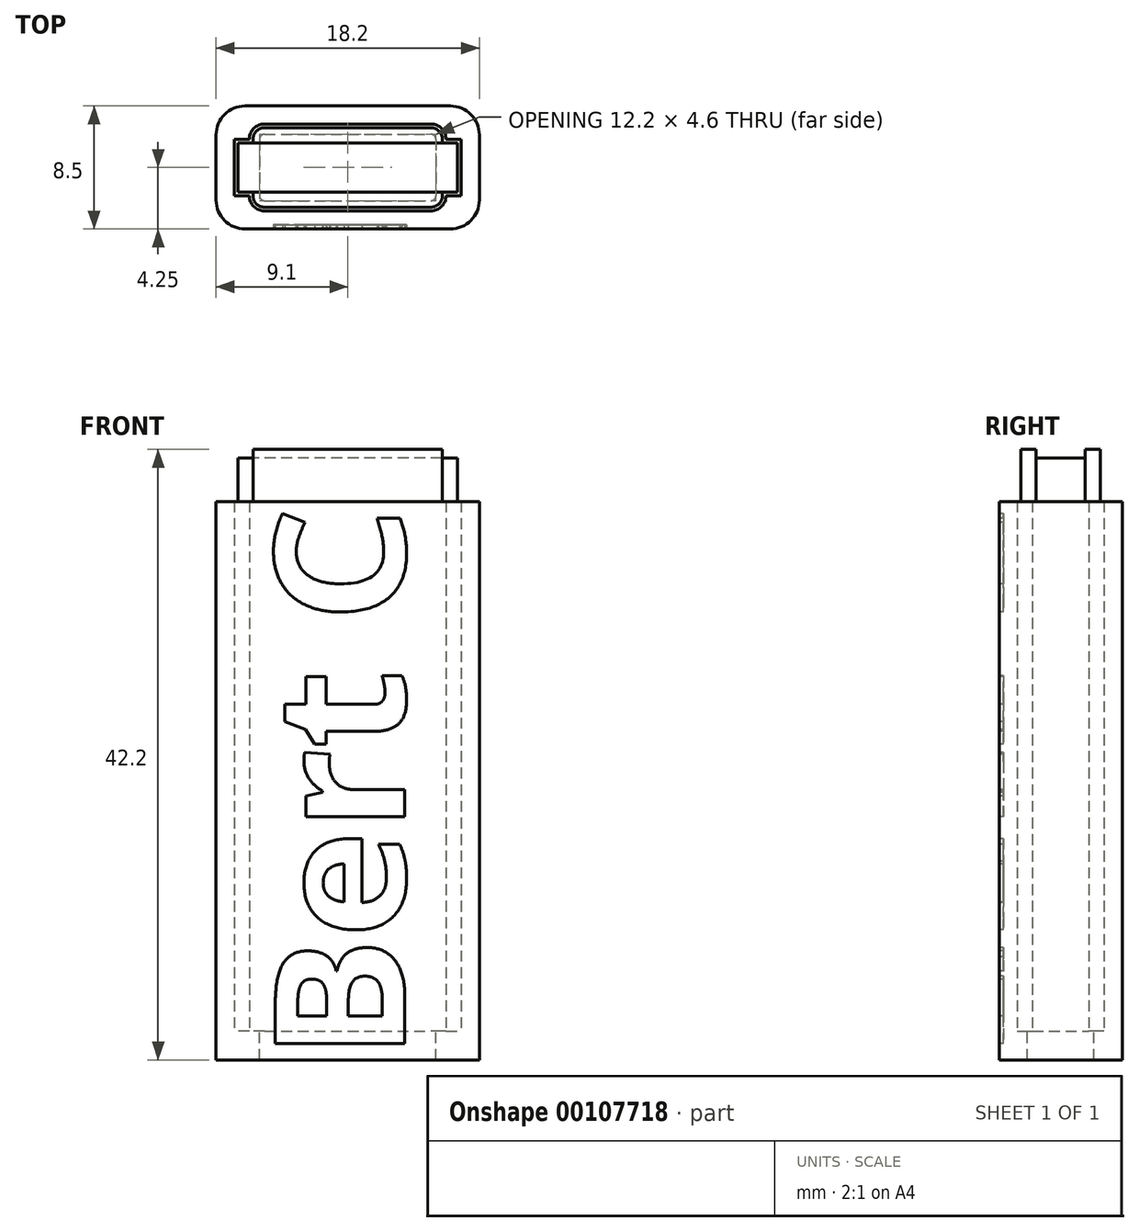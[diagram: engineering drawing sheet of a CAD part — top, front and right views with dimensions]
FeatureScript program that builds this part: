
annotation { "Feature Type Name" : "Feature", "Feature Type Description" : "" }
export const myFeature = defineFeature(function(context is Context, id is Id, definition is map)
    precondition{}
    {
        {
            var Q0;
            Q0=qCreatedBy(makeId("Top.planeOp"),FACE);
            var sketch = newSketch(context, id + "F0", { "sketchPlane" : qUnion([Q0])});
            skLineSegment(sketch, "E0.bottom", {"start": v(-5.75, 2.1) * mm, "end": v(5.75, 2.1) * mm});
            skLineSegment(sketch, "E0.top", {"start": v(-5.75, -2.3) * mm, "end": v(5.75, -2.3) * mm});
            skLineSegment(sketch, "E0.left", {"start": v(-6, 1.85) * mm, "end": v(-6, 0.2) * mm});
            skLineSegment(sketch, "E0.right", {"start": v(6, 1.85) * mm, "end": v(6, 0.2) * mm});
            skPoint(sketch, "E1.visualSharp", {"position": v(-6, 2.1) * mm});
            skArc(sketch, "E1.filletArc", {"start": v(-5.75, 2.1) * mm, "mid": v(-5.93, 2.03) * mm, "end": v(-6, 1.85) * mm});
            skPoint(sketch, "E2.visualSharp", {"position": v(-6, -2.3) * mm});
            skArc(sketch, "E2.filletArc", {"start": v(-6, -2.05) * mm, "mid": v(-5.93, -2.23) * mm, "end": v(-5.75, -2.3) * mm});
            skPoint(sketch, "E3.visualSharp", {"position": v(6, 2.1) * mm});
            skArc(sketch, "E3.filletArc", {"start": v(6, 1.85) * mm, "mid": v(5.93, 2.03) * mm, "end": v(5.75, 2.1) * mm});
            skPoint(sketch, "E4.visualSharp", {"position": v(6, -2.3) * mm});
            skArc(sketch, "E4.filletArc", {"start": v(5.75, -2.3) * mm, "mid": v(5.93, -2.23) * mm, "end": v(6, -2.05) * mm});
            skPoint(sketch, "E5", {"position": v(-6, -0.1) * mm});
            skPoint(sketch, "E6", {"position": v(6, -0.1) * mm});
            skLineSegment(sketch, "E7", {"start": v(-6, -0.1) * mm, "end": v(-7.05, -0.1) * mm});
            skLineSegment(sketch, "E8", {"start": v(6, -0.1) * mm, "end": v(7.05, -0.1) * mm});
            skLineSegment(sketch, "E9", {"start": v(-7.05, -0.1) * mm, "end": v(-7.05, 0.2) * mm});
            skLineSegment(sketch, "E10", {"start": v(-7.05, 0.2) * mm, "end": v(-6, 0.2) * mm});
            skLineSegment(sketch, "E11", {"start": v(-7.05, -0.1) * mm, "end": v(-7.05, -0.4) * mm});
            skLineSegment(sketch, "E12", {"start": v(-7.05, -0.4) * mm, "end": v(-6, -0.4) * mm});
            skLineSegment(sketch, "E13", {"start": v(7.05, -0.1) * mm, "end": v(7.05, -0.4) * mm});
            skLineSegment(sketch, "E14", {"start": v(7.05, -0.4) * mm, "end": v(6, -0.4) * mm});
            skLineSegment(sketch, "E15", {"start": v(7.05, -0.1) * mm, "end": v(7.05, 0.2) * mm});
            skLineSegment(sketch, "E16", {"start": v(7.05, 0.2) * mm, "end": v(6, 0.2) * mm});
            skPoint(sketch, "E17.end.orphan", {"position": v(-7.05, 2.1) * mm});
            skPoint(sketch, "E18.orphan", {"position": v(-7.05, -2.3) * mm});
            skPoint(sketch, "E19.end.orphan", {"position": v(7.05, 2.1) * mm});
            skPoint(sketch, "E20.orphan", {"position": v(7.05, -2.3) * mm});
            skLineSegment(sketch, "E21", {"start": v(-6, 0.2) * mm, "end": v(-6, -0.4) * mm});
            skLineSegment(sketch, "E22", {"start": v(-6, -0.4) * mm, "end": v(-6, -2.05) * mm});
            skLineSegment(sketch, "E23", {"start": v(6, -0.4) * mm, "end": v(6, -2.05) * mm});
            skLineSegment(sketch, "E24", {"start": v(6, 0.2) * mm, "end": v(6, -0.4) * mm});
            skArc(sketch, "E25.0", {"start": v(-5.75, 2.9) * mm, "mid": v(-6.5, 2.6) * mm, "end": v(-6.8, 1.85) * mm});
            skLineSegment(sketch, "E25.1", {"start": v(-5.75, 2.9) * mm, "end": v(5.75, 2.9) * mm});
            skArc(sketch, "E25.2", {"start": v(6.8, 1.85) * mm, "mid": v(6.5, 2.6) * mm, "end": v(5.75, 2.9) * mm});
            skLineSegment(sketch, "E25.3", {"start": v(6.8, 1.85) * mm, "end": v(6.8, 1) * mm});
            skLineSegment(sketch, "E25.5", {"start": v(-6.8, 1.85) * mm, "end": v(-6.8, 1) * mm});
            skLineSegment(sketch, "E25.6", {"start": v(7.85, 0) * mm, "end": v(7.85, 1.85) * mm});
            skLineSegment(sketch, "E25.7", {"start": v(7.85, 0) * mm, "end": v(7.85, -2.05) * mm});
            skLineSegment(sketch, "E25.9", {"start": v(-7.85, 0) * mm, "end": v(-7.85, -2.05) * mm});
            skLineSegment(sketch, "E25.10", {"start": v(-7.85, 0) * mm, "end": v(-7.85, 1.85) * mm});
            skLineSegment(sketch, "E25.12", {"start": v(-6.8, -1.2) * mm, "end": v(-6.8, -2.05) * mm});
            skArc(sketch, "E25.13", {"start": v(-6.8, -2.05) * mm, "mid": v(-6.5, -2.8) * mm, "end": v(-5.75, -3.1) * mm});
            skLineSegment(sketch, "E25.14", {"start": v(-5.75, -3.1) * mm, "end": v(5.75, -3.1) * mm});
            skArc(sketch, "E25.15", {"start": v(5.75, -3.1) * mm, "mid": v(6.5, -2.8) * mm, "end": v(6.8, -2.05) * mm});
            skLineSegment(sketch, "E25.16", {"start": v(6.8, -1.2) * mm, "end": v(6.8, -2.05) * mm});
            skLineSegment(sketch, "E26.0", {"start": v(-7.1, -4.35) * mm, "end": v(7.1, -4.35) * mm});
            skLineSegment(sketch, "E27.0", {"start": v(-7.1, 4.15) * mm, "end": v(7.1, 4.15) * mm});
            skLineSegment(sketch, "E28.0", {"start": v(-9.1, -2.35) * mm, "end": v(-9.1, 2.15) * mm});
            skLineSegment(sketch, "E29.0", {"start": v(9.1, -2.35) * mm, "end": v(9.1, 2.15) * mm});
            skPoint(sketch, "E30.visualSharp", {"position": v(-9.1, 4.15) * mm});
            skArc(sketch, "E30.filletArc", {"start": v(-7.1, 4.15) * mm, "mid": v(-8.51, 3.56) * mm, "end": v(-9.1, 2.15) * mm});
            skPoint(sketch, "E31.visualSharp", {"position": v(-9.1, -4.35) * mm});
            skArc(sketch, "E31.filletArc", {"start": v(-9.1, -2.35) * mm, "mid": v(-8.51, -3.76) * mm, "end": v(-7.1, -4.35) * mm});
            skPoint(sketch, "E32.visualSharp", {"position": v(9.1, -4.35) * mm});
            skArc(sketch, "E32.filletArc", {"start": v(7.1, -4.35) * mm, "mid": v(8.51, -3.76) * mm, "end": v(9.1, -2.35) * mm});
            skPoint(sketch, "E33.visualSharp", {"position": v(9.1, 4.15) * mm});
            skArc(sketch, "E33.filletArc", {"start": v(9.1, 2.15) * mm, "mid": v(8.51, 3.56) * mm, "end": v(7.1, 4.15) * mm});
            skLineSegment(sketch, "E34", {"start": v(-6.8, 1) * mm, "end": v(-6.8, -1.2) * mm});
            skLineSegment(sketch, "E35", {"start": v(6.8, 1) * mm, "end": v(6.8, -1.2) * mm});
            skArc(sketch, "E36.0", {"start": v(-6.1, -2.05) * mm, "mid": v(-6, -2.3) * mm, "end": v(-5.75, -2.4) * mm});
            skLineSegment(sketch, "E36.1", {"start": v(6.1, 1.85) * mm, "end": v(6.1, 0.4) * mm});
            skLineSegment(sketch, "E36.2", {"start": v(6.1, 0.4) * mm, "end": v(6.1, -0.4) * mm});
            skLineSegment(sketch, "E36.3", {"start": v(6.1, -0.4) * mm, "end": v(6.1, -2.05) * mm});
            skArc(sketch, "E36.4", {"start": v(5.75, -2.4) * mm, "mid": v(6, -2.3) * mm, "end": v(6.1, -2.05) * mm});
            skArc(sketch, "E36.5", {"start": v(6.1, 1.85) * mm, "mid": v(6, 2.1) * mm, "end": v(5.75, 2.2) * mm});
            skLineSegment(sketch, "E36.6", {"start": v(-5.75, -2.4) * mm, "end": v(5.75, -2.4) * mm});
            skLineSegment(sketch, "E36.7", {"start": v(-5.75, 2.2) * mm, "end": v(5.75, 2.2) * mm});
            skArc(sketch, "E36.8", {"start": v(-5.75, 2.2) * mm, "mid": v(-6, 2.1) * mm, "end": v(-6.1, 1.85) * mm});
            skLineSegment(sketch, "E36.9", {"start": v(-6.1, 1.85) * mm, "end": v(-6.1, 0.4) * mm});
            skLineSegment(sketch, "E36.10", {"start": v(-6.1, 0.4) * mm, "end": v(-6.1, -0.4) * mm});
            skLineSegment(sketch, "E36.11", {"start": v(-6.1, -0.4) * mm, "end": v(-6.1, -2.05) * mm});
            skLineSegment(sketch, "E37", {"start": v(-6.8, -2.05) * mm, "end": v(-7.85, -2.05) * mm});
            skLineSegment(sketch, "E38", {"start": v(-6.8, 1.85) * mm, "end": v(-7.85, 1.85) * mm});
            skLineSegment(sketch, "E39", {"start": v(6.8, 1.85) * mm, "end": v(7.85, 1.85) * mm});
            skLineSegment(sketch, "E40", {"start": v(6.8, -2.05) * mm, "end": v(7.85, -2.05) * mm});
            skPoint(sketch, "E41.orphan", {"position": v(-7.85, -1.2) * mm});
            skPoint(sketch, "E42.orphan", {"position": v(-7.85, 1) * mm});
            skPoint(sketch, "E43.orphan", {"position": v(7.85, 1) * mm});
            skPoint(sketch, "E44.orphan", {"position": v(7.85, -1.2) * mm});
            skSolve(sketch);
        }
        {
            var Q0;
            Q0=makeQuery(id+"F0.imprint","IMPRINT",FACE,{"disambiguationData":[TD([[makeQuery(id+"F0.imprint","IMPRINT",EDGE,{"derivedFrom":sQuery(id+"F0.wireOp",EDGE,"E25.0")}),-1.0]])]});
            extrude(context, id + "F1", {"entities" : qUnion([Q0]), "depth" : 36.6 * mm});
        }
        {
            var Q0;
            {var subQ4=sQuery(id+"F0.wireOp",EDGE,"E9");Q0=makeQuery(id+"F0.imprint","IMPRINT",FACE,{"disambiguationData":[TD([[makeQuery(id+"F0.imprint","IMPRINT",EDGE,{"derivedFrom":subQ4}),1.0]])]});}
            var Q1;
            {var subQ0=sQuery(id+"F0.wireOp",EDGE,"E9");Q1=makeQuery(id+"F0.imprint","IMPRINT",FACE,{"disambiguationData":[TD([[makeQuery(id+"F0.imprint","IMPRINT",EDGE,{"derivedFrom":subQ0}),-1.0]])]});}
            var Q2;
            {var subQ0=sQuery(id+"F0.wireOp",EDGE,"E11");Q2=makeQuery(id+"F0.imprint","IMPRINT",FACE,{"disambiguationData":[TD([[makeQuery(id+"F0.imprint","IMPRINT",EDGE,{"derivedFrom":subQ0}),1.0]])]});}
            var Q3;
            {var subQ0=sQuery(id+"F0.wireOp",EDGE,"E15");Q3=makeQuery(id+"F0.imprint","IMPRINT",FACE,{"disambiguationData":[TD([[makeQuery(id+"F0.imprint","IMPRINT",EDGE,{"derivedFrom":subQ0}),1.0]])]});}
            var Q4;
            {var subQ0=sQuery(id+"F0.wireOp",EDGE,"E13");Q4=makeQuery(id+"F0.imprint","IMPRINT",FACE,{"disambiguationData":[TD([[makeQuery(id+"F0.imprint","IMPRINT",EDGE,{"derivedFrom":subQ0}),-1.0]])]});}
            var Q5;
            {var subQ7=sQuery(id+"F0.wireOp",EDGE,"E13");Q5=makeQuery(id+"F0.imprint","IMPRINT",FACE,{"disambiguationData":[TD([[makeQuery(id+"F0.imprint","IMPRINT",EDGE,{"derivedFrom":subQ7}),1.0]])]});}
            var Q6;
            Q6=makeQuery(id+"F0.imprint","IMPRINT",FACE,{"disambiguationData":[TD([[makeQuery(id+"F0.imprint","IMPRINT",EDGE,{"derivedFrom":sQuery(id+"F0.wireOp",EDGE,"E25.0")}),-1.0]])]});
            var Q7;
            {var subQ1=sQuery(id+"F0.wireOp",EDGE,"E25.12");Q7=makeQuery(id+"F0.imprint","IMPRINT",FACE,{"disambiguationData":[TD([[makeQuery(id+"F0.imprint","IMPRINT",EDGE,{"derivedFrom":subQ1}),1.0]])]});}
            var Q8;
            {var subQ0=sQuery(id+"F0.wireOp",EDGE,"E36.10");var subQ1=sQuery(id+"F0.wireOp",EDGE,"E7");var subQ2=makeQuery(id+"F0.imprint","INTERSECT",VERTEX,{"derivedFrom":[subQ1,subQ0]});Q8=makeQuery(id+"F0.imprint","IMPRINT",FACE,{"disambiguationData":[TD([[makeQuery(id+"F0.imprint","IMPRINT",EDGE,{"disambiguationData":[TD([[subQ2,-1.0]])],"derivedFrom":subQ1}),1.0]])]});}
            var Q9;
            {var subQ0=sQuery(id+"F0.wireOp",EDGE,"E36.10");var subQ1=sQuery(id+"F0.wireOp",EDGE,"E7");var subQ2=makeQuery(id+"F0.imprint","INTERSECT",VERTEX,{"derivedFrom":[subQ1,subQ0]});Q9=makeQuery(id+"F0.imprint","IMPRINT",FACE,{"disambiguationData":[TD([[makeQuery(id+"F0.imprint","IMPRINT",EDGE,{"disambiguationData":[TD([[subQ2,-1.0]])],"derivedFrom":subQ1}),-1.0]])]});}
            var Q10;
            Q10=makeQuery(id+"F0.imprint","IMPRINT",FACE,{"disambiguationData":[TD([[makeQuery(id+"F0.imprint","IMPRINT",EDGE,{"derivedFrom":sQuery(id+"F0.wireOp",EDGE,"E25.0")}),1.0]])]});
            var Q11;
            {var subQ0=sQuery(id+"F0.wireOp",EDGE,"E36.2");var subQ1=sQuery(id+"F0.wireOp",EDGE,"E8");var subQ2=makeQuery(id+"F0.imprint","INTERSECT",VERTEX,{"derivedFrom":[subQ1,subQ0]});Q11=makeQuery(id+"F0.imprint","IMPRINT",FACE,{"disambiguationData":[TD([[makeQuery(id+"F0.imprint","IMPRINT",EDGE,{"disambiguationData":[TD([[subQ2,-1.0]])],"derivedFrom":subQ1}),1.0]])]});}
            var Q12;
            {var subQ0=sQuery(id+"F0.wireOp",EDGE,"E36.2");var subQ1=sQuery(id+"F0.wireOp",EDGE,"E8");var subQ2=makeQuery(id+"F0.imprint","INTERSECT",VERTEX,{"derivedFrom":[subQ1,subQ0]});Q12=makeQuery(id+"F0.imprint","IMPRINT",FACE,{"disambiguationData":[TD([[makeQuery(id+"F0.imprint","IMPRINT",EDGE,{"disambiguationData":[TD([[subQ2,-1.0]])],"derivedFrom":subQ1}),-1.0]])]});}
            extrude(context, id + "F2", {"entities" : qUnion([Q0, Q1, Q2, Q3, Q4, Q5, Q6, Q7, Q8, Q9, Q10, Q11, Q12]), "operationType" : NewBodyOperationType.ADD, "oppositeDirection" : true, "depth" : 2 * mm});
        }
        {
            var Q0;
            {var subQ0=sQuery(id+"F0.wireOp",EDGE,"E26.0");Q0=makeQuery(id+"F2.boolean.opBoolean","MERGE",FACE,{"derivedFrom":[makeQuery(id+"F1.opExtrude","SWEPT_FACE",FACE,{"disambiguationData":[OSD([subQ0])]}),makeQuery(id+"F2.opExtrude","SWEPT_FACE",FACE,{"disambiguationData":[OSD([subQ0])]})]});}
            var sketch = newSketch(context, id + "F3", { "sketchPlane" : qUnion([Q0])});
            skLineSegment(sketch, "E45.1", {"start": v(-7.1, 36.6) * mm, "end": v(7.1, 36.6) * mm});
            skLineSegment(sketch, "E45.2", {"start": v(-7.1, 36.6) * mm, "end": v(-7.1, -2) * mm});
            skLineSegment(sketch, "E45.3", {"start": v(7.1, 36.6) * mm, "end": v(7.1, -2) * mm});
            skLineSegment(sketch, "E45.4", {"start": v(-7.1, -2) * mm, "end": v(7.1, -2) * mm});
            skText(sketch, "E46", { "text": "Bert C\n", "fontName": "OpenSans-Bold.ttf"});
            const initialGuessF3  = {"E46": [0.00395, -0.002, 0, 1, 0.00903]};
            skSetInitialGuess(sketch, initialGuessF3);
            skSolve(sketch);
        }
        {
            var Q0;
            Q0=makeQuery(id+"F3.imprint","IMPRINT",FACE,{"disambiguationData":[TD([[makeQuery(id+"F3.imprint","IMPRINT",EDGE,{"derivedFrom":sQuery(id+"F3.wireOp",EDGE,"E46.sketch_text.stroke-76")}),-1.0]])]});
            var Q1;
            Q1=makeQuery(id+"F3.imprint","IMPRINT",FACE,{"disambiguationData":[TD([[makeQuery(id+"F3.imprint","IMPRINT",EDGE,{"derivedFrom":sQuery(id+"F3.wireOp",EDGE,"E46.sketch_text.stroke-58")}),-1.0]])]});
            var Q2;
            Q2=makeQuery(id+"F3.imprint","IMPRINT",FACE,{"disambiguationData":[TD([[makeQuery(id+"F3.imprint","IMPRINT",EDGE,{"derivedFrom":sQuery(id+"F3.wireOp",EDGE,"E46.sketch_text.stroke-45")}),-1.0]])]});
            var Q3;
            Q3=makeQuery(id+"F3.imprint","IMPRINT",FACE,{"disambiguationData":[TD([[makeQuery(id+"F3.imprint","IMPRINT",EDGE,{"derivedFrom":sQuery(id+"F3.wireOp",EDGE,"E46.sketch_text.stroke-25")}),-1.0]])]});
            var Q4;
            Q4=makeQuery(id+"F3.imprint","IMPRINT",FACE,{"disambiguationData":[TD([[makeQuery(id+"F3.imprint","IMPRINT",EDGE,{"derivedFrom":sQuery(id+"F3.wireOp",EDGE,"E46.sketch_text.stroke-0")}),-1.0]])]});
            var Q5;
            Q5=makeQuery(id+"F3.imprint","IMPRINT",FACE,{"disambiguationData":[TD([[makeQuery(id+"F3.imprint","IMPRINT",EDGE,{"derivedFrom":sQuery(id+"F3.wireOp",EDGE,"E46.sketch_text.stroke-79")}),-1.0]])]});
            var Q6;
            Q6=makeQuery(id+"F3.imprint","IMPRINT",FACE,{"disambiguationData":[TD([[makeQuery(id+"F3.imprint","IMPRINT",EDGE,{"derivedFrom":sQuery(id+"F3.wireOp",EDGE,"E46.sketch_text.stroke-96")}),-1.0]])]});
            extrude(context, id + "F4", {"entities" : qUnion([Q0, Q1, Q2, Q3, Q4, Q5, Q6]), "operationType" : NewBodyOperationType.REMOVE, "oppositeDirection" : true, "depth" : .3 * mm});
        }
        {
            var Q0;
            Q0=makeQuery(id+"F1.opExtrude","CAP_FACE",FACE,{"disambiguationData":[OSD([sQuery(id+"F0.wireOp",EDGE,"E25.0"),sQuery(id+"F0.wireOp",EDGE,"E25.1"),sQuery(id+"F0.wireOp",EDGE,"E25.2"),sQuery(id+"F0.wireOp",EDGE,"E25.6"),sQuery(id+"F0.wireOp",EDGE,"E25.7"),sQuery(id+"F0.wireOp",EDGE,"E25.9"),sQuery(id+"F0.wireOp",EDGE,"E25.10"),sQuery(id+"F0.wireOp",EDGE,"E25.13"),sQuery(id+"F0.wireOp",EDGE,"E25.14"),sQuery(id+"F0.wireOp",EDGE,"E25.15"),sQuery(id+"F0.wireOp",EDGE,"E26.0"),sQuery(id+"F0.wireOp",EDGE,"E27.0"),sQuery(id+"F0.wireOp",EDGE,"E28.0"),sQuery(id+"F0.wireOp",EDGE,"E29.0"),sQuery(id+"F0.wireOp",EDGE,"E30.filletArc"),sQuery(id+"F0.wireOp",EDGE,"E31.filletArc"),sQuery(id+"F0.wireOp",EDGE,"E32.filletArc"),sQuery(id+"F0.wireOp",EDGE,"E33.filletArc"),sQuery(id+"F0.wireOp",EDGE,"E37"),sQuery(id+"F0.wireOp",EDGE,"E38"),sQuery(id+"F0.wireOp",EDGE,"E39"),sQuery(id+"F0.wireOp",EDGE,"E40")])],"isStart":false});
            var sketch = newSketch(context, id + "F5", { "sketchPlane" : qUnion([Q0])});
            skLineSegment(sketch, "E47.0", {"start": v(-6.8, -2.05) * mm, "end": v(-7.85, -2.05) * mm});
            skLineSegment(sketch, "E47.1", {"start": v(-7.85, 1.85) * mm, "end": v(-7.85, -2.05) * mm});
            skLineSegment(sketch, "E47.2", {"start": v(-6.8, 1.85) * mm, "end": v(-7.85, 1.85) * mm});
            skArc(sketch, "E47.3", {"start": v(-5.75, 2.9) * mm, "mid": v(-6.5, 2.6) * mm, "end": v(-6.8, 1.85) * mm});
            skLineSegment(sketch, "E47.4", {"start": v(-5.75, 2.9) * mm, "end": v(5.75, 2.9) * mm});
            skArc(sketch, "E47.5", {"start": v(6.8, 1.85) * mm, "mid": v(6.5, 2.6) * mm, "end": v(5.75, 2.9) * mm});
            skLineSegment(sketch, "E47.6", {"start": v(6.8, 1.85) * mm, "end": v(7.85, 1.85) * mm});
            skLineSegment(sketch, "E47.7", {"start": v(7.85, -2.05) * mm, "end": v(7.85, 1.85) * mm});
            skLineSegment(sketch, "E47.8", {"start": v(6.8, -2.05) * mm, "end": v(7.85, -2.05) * mm});
            skArc(sketch, "E47.9", {"start": v(5.75, -3.1) * mm, "mid": v(6.5, -2.8) * mm, "end": v(6.8, -2.05) * mm});
            skLineSegment(sketch, "E47.10", {"start": v(-5.75, -3.1) * mm, "end": v(5.75, -3.1) * mm});
            skArc(sketch, "E47.11", {"start": v(-6.8, -2.05) * mm, "mid": v(-6.5, -2.8) * mm, "end": v(-5.75, -3.1) * mm});
            skArc(sketch, "E48.0", {"start": v(-6.5, -1.8) * mm, "mid": v(-6.4, -2.52) * mm, "end": v(-5.75, -2.85) * mm});
            skLineSegment(sketch, "E48.1", {"start": v(6.5, 1.6) * mm, "end": v(7.6, 1.6) * mm});
            skLineSegment(sketch, "E48.2", {"start": v(7.6, -1.8) * mm, "end": v(7.6, 1.6) * mm});
            skLineSegment(sketch, "E48.3", {"start": v(6.5, -1.8) * mm, "end": v(7.6, -1.8) * mm});
            skArc(sketch, "E48.4", {"start": v(5.75, -2.85) * mm, "mid": v(6.4, -2.52) * mm, "end": v(6.5, -1.8) * mm});
            skArc(sketch, "E48.5", {"start": v(6.5, 1.6) * mm, "mid": v(6.4, 2.32) * mm, "end": v(5.75, 2.65) * mm});
            skLineSegment(sketch, "E48.6", {"start": v(-5.75, -2.85) * mm, "end": v(5.75, -2.85) * mm});
            skLineSegment(sketch, "E48.7", {"start": v(-5.75, 2.65) * mm, "end": v(5.75, 2.65) * mm});
            skArc(sketch, "E48.8", {"start": v(-5.75, 2.65) * mm, "mid": v(-6.4, 2.32) * mm, "end": v(-6.5, 1.6) * mm});
            skLineSegment(sketch, "E48.9", {"start": v(-6.5, 1.6) * mm, "end": v(-7.6, 1.6) * mm});
            skLineSegment(sketch, "E48.10", {"start": v(-7.6, 1.6) * mm, "end": v(-7.6, -1.8) * mm});
            skLineSegment(sketch, "E48.11", {"start": v(-6.5, -1.8) * mm, "end": v(-7.6, -1.8) * mm});
            skLineSegment(sketch, "E49", {"start": v(-6.5, 1.6) * mm, "end": v(6.5, 1.6) * mm});
            skLineSegment(sketch, "E50", {"start": v(-6.5, -1.8) * mm, "end": v(6.5, -1.8) * mm});
            skSolve(sketch);
        }
        {
            var Q0;
            Q0=makeQuery(id+"F5.imprint","IMPRINT",FACE,{"disambiguationData":[TD([[makeQuery(id+"F5.imprint","IMPRINT",EDGE,{"derivedFrom":sQuery(id+"F5.wireOp",EDGE,"E48.0")}),1.0]])]});
            var Q1;
            Q1=makeQuery(id+"F5.imprint","IMPRINT",FACE,{"disambiguationData":[TD([[makeQuery(id+"F5.imprint","IMPRINT",EDGE,{"derivedFrom":sQuery(id+"F5.wireOp",EDGE,"E48.1")}),-1.0]])]});
            var Q2;
            Q2=makeQuery(id+"F5.imprint","IMPRINT",FACE,{"disambiguationData":[TD([[makeQuery(id+"F5.imprint","IMPRINT",EDGE,{"derivedFrom":sQuery(id+"F5.wireOp",EDGE,"E48.5")}),1.0]])]});
            extrude(context, id + "F6", {"entities" : qUnion([Q0, Q1, Q2]), "depth" : 3 * mm});
        }
        {
            var Q0;
            Q0=makeQuery(id+"F5.imprint","IMPRINT",FACE,{"disambiguationData":[TD([[makeQuery(id+"F5.imprint","IMPRINT",EDGE,{"derivedFrom":sQuery(id+"F5.wireOp",EDGE,"E48.0")}),1.0]])]});
            var Q1;
            Q1=makeQuery(id+"F5.imprint","IMPRINT",FACE,{"disambiguationData":[TD([[makeQuery(id+"F5.imprint","IMPRINT",EDGE,{"derivedFrom":sQuery(id+"F5.wireOp",EDGE,"E48.5")}),1.0]])]});
            extrude(context, id + "F7", {"entities" : qUnion([Q0, Q1]), "operationType" : NewBodyOperationType.ADD, "depth" : 3.6 * mm});
        }
    });
